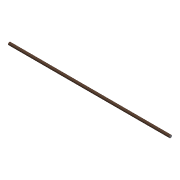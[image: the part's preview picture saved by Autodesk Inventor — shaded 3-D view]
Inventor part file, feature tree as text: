
AUTODESK INVENTOR PART (.ipt)
format: ipt  version: 2016 (Build 200138000, 138)  size: 94,208 bytes
history: native  units: in
note: dims shown in document units (in); Inventor stores cm internally (conversion verified against a paired STEP export)
features: extrude x1, sketch x1
ambient origin geometry x8: Origin, YZ Plane, XZ Plane, XY Plane, X Axis, Y Axis, Z Axis, Center Point
bodies: Body1 (feature_tree)
feature tree (2):
  extrude  "Extrusion2"  Depth=23.622in TaperAngle=0.0deg
  sketch  "Sketch2"  dims[d3=0.3937in d4=23.622in d5=0.0in]
